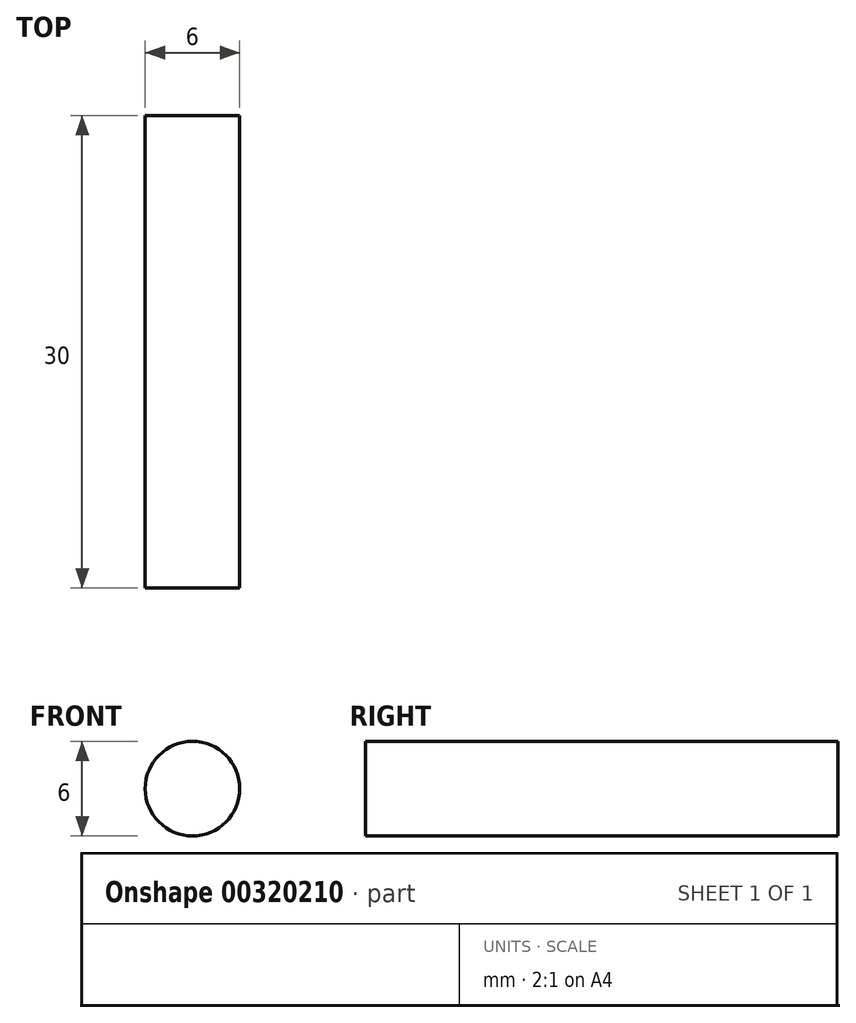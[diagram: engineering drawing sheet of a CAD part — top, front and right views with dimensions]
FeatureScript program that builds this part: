
annotation { "Feature Type Name" : "Feature", "Feature Type Description" : "" }
export const myFeature = defineFeature(function(context is Context, id is Id, definition is map)
    precondition{}
    {
        {
            var Q0;
            Q0=qCreatedBy(makeId("Front.planeOp"),FACE);
            var sketch = newSketch(context, id + "F0", { "sketchPlane" : qUnion([Q0])});
            skCircle(sketch, "E0", {"center": v(0, 0) * mm, "radius": 3 * mm});
            skSolve(sketch);
        }
        {
            var Q0;
            Q0=qSketchRegion(id+"F0",true);
            extrude(context, id + "F1", {"entities" : qUnion([Q0]), "endBound" : BoundingType.SYMMETRIC, "depth" : 30 * mm});
        }
    });
